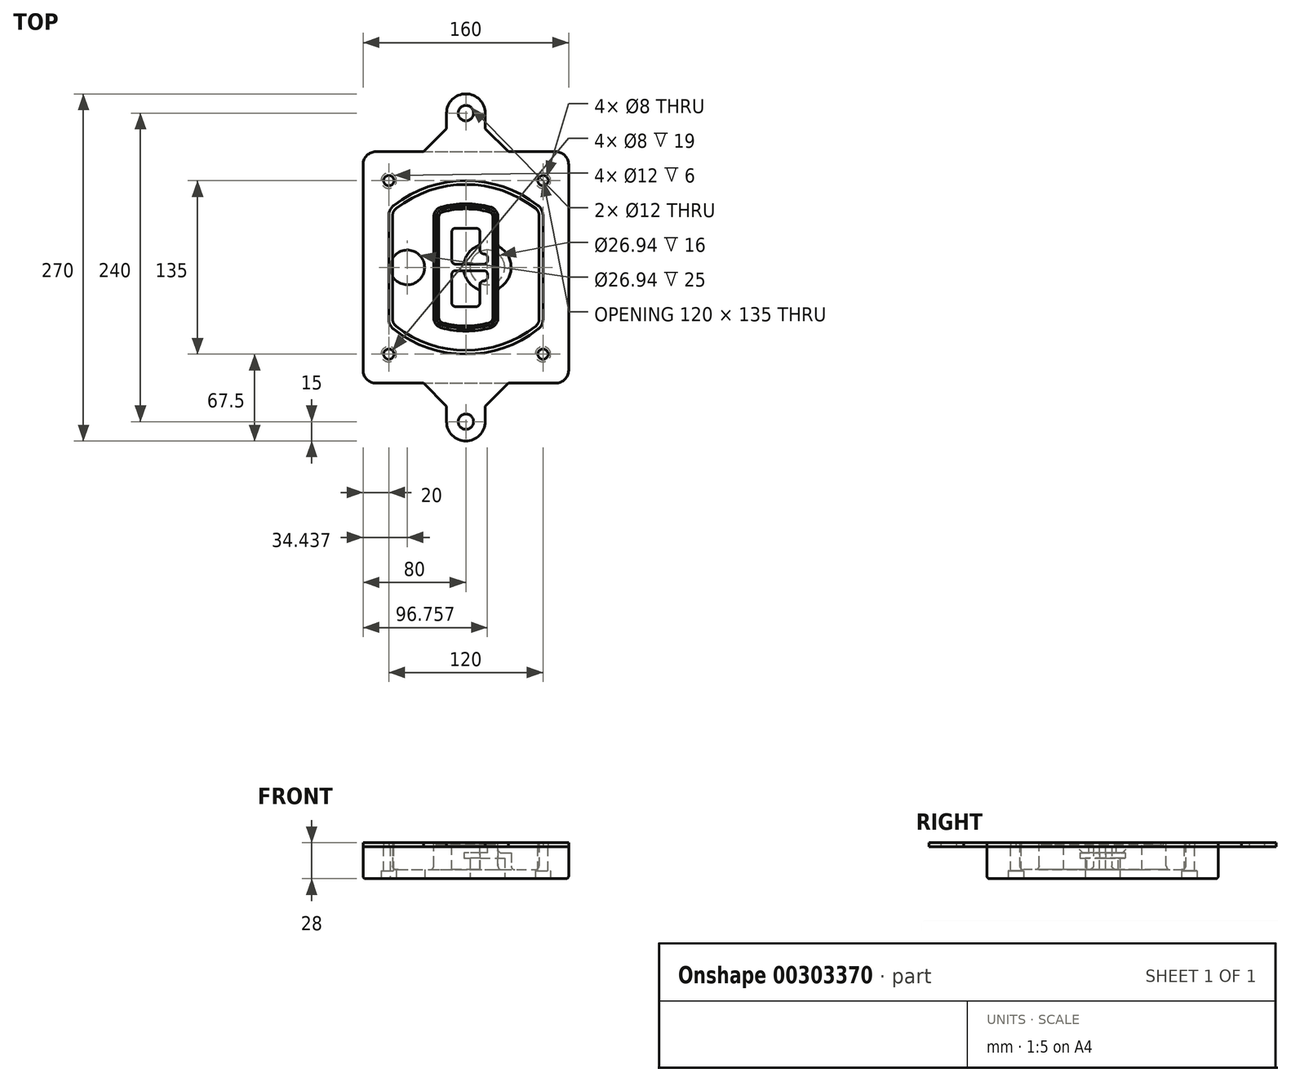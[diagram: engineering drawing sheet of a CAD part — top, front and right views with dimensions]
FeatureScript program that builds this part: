
annotation { "Feature Type Name" : "Feature", "Feature Type Description" : "" }
export const myFeature = defineFeature(function(context is Context, id is Id, definition is map)
    precondition{}
    {
        {
            var Q0;
            Q0=qCreatedBy(makeId("Top.planeOp"),FACE);
            var sketch = newSketch(context, id + "F0", { "sketchPlane" : qUnion([Q0])});
            skPoint(sketch, "E0.rect.middle", {"position": v(0, 0) * mm});
            skLineSegment(sketch, "E1.bottom", {"start": v(-70, -90) * mm, "end": v(70, -90) * mm});
            skLineSegment(sketch, "E1.top", {"start": v(-70, 90) * mm, "end": v(70, 90) * mm});
            skLineSegment(sketch, "E1.left", {"start": v(-80, -80) * mm, "end": v(-80, 80) * mm});
            skLineSegment(sketch, "E1.right", {"start": v(80, -80) * mm, "end": v(80, 80) * mm});
            skLineSegment(sketch, "E2", {"start": v(-80, 90) * mm, "end": v(80, -90) * mm, "construction": true});
            skLineSegment(sketch, "E3", {"start": v(80, 90) * mm, "end": v(-80, -90) * mm, "construction": true});
            skCircle(sketch, "E4", {"center": v(-60, 67.5) * mm, "radius": 4 * mm});
            skCircle(sketch, "E5", {"center": v(60, 67.5) * mm, "radius": 4 * mm});
            skCircle(sketch, "E6", {"center": v(60, -67.5) * mm, "radius": 4 * mm});
            skCircle(sketch, "E7", {"center": v(-60, -67.5) * mm, "radius": 4 * mm});
            skLineSegment(sketch, "E8", {"start": v(-60, 67.5) * mm, "end": v(60, 67.5) * mm, "construction": true});
            skLineSegment(sketch, "E9", {"start": v(60, 67.5) * mm, "end": v(60, -67.5) * mm, "construction": true});
            skLineSegment(sketch, "E10", {"start": v(60, -67.5) * mm, "end": v(-60, -67.5) * mm, "construction": true});
            skLineSegment(sketch, "E11", {"start": v(-60, -67.5) * mm, "end": v(-60, 67.5) * mm, "construction": true});
            skLineSegment(sketch, "E12", {"start": v(-60, 40.3) * mm, "end": v(-60, -40.3) * mm});
            skLineSegment(sketch, "E13", {"start": v(60, 40.3) * mm, "end": v(60, -40.3) * mm});
            skArc(sketch, "E14", {"start": v(56.15, 48.18) * mm, "mid": v(0, 67.5) * mm, "end": v(-56.15, 48.18) * mm});
            skArc(sketch, "E15", {"start": v(-56.15, -48.18) * mm, "mid": v(0, -67.5) * mm, "end": v(56.15, -48.18) * mm});
            skLineSegment(sketch, "E16", {"start": v(-60, 0) * mm, "end": v(60, 0) * mm, "construction": true});
            skPoint(sketch, "E17.visualSharp", {"position": v(-60, -45) * mm});
            skArc(sketch, "E17.filletArc", {"start": v(-60, -40.3) * mm, "mid": v(-58.99, -44.68) * mm, "end": v(-56.15, -48.18) * mm});
            skPoint(sketch, "E18.visualSharp", {"position": v(-60, 45) * mm});
            skArc(sketch, "E18.filletArc", {"start": v(-56.15, 48.18) * mm, "mid": v(-58.99, 44.68) * mm, "end": v(-60, 40.3) * mm});
            skPoint(sketch, "E19.visualSharp", {"position": v(60, 45) * mm});
            skArc(sketch, "E19.filletArc", {"start": v(60, 40.3) * mm, "mid": v(58.99, 44.68) * mm, "end": v(56.15, 48.18) * mm});
            skPoint(sketch, "E20.visualSharp", {"position": v(60, -45) * mm});
            skArc(sketch, "E20.filletArc", {"start": v(56.15, -48.18) * mm, "mid": v(58.99, -44.68) * mm, "end": v(60, -40.3) * mm});
            skPoint(sketch, "E21.visualSharp", {"position": v(-80, 90) * mm});
            skArc(sketch, "E21.filletArc", {"start": v(-70, 90) * mm, "mid": v(-77.07, 87.07) * mm, "end": v(-80, 80) * mm});
            skPoint(sketch, "E22.visualSharp", {"position": v(80, 90) * mm});
            skArc(sketch, "E22.filletArc", {"start": v(80, 80) * mm, "mid": v(77.07, 87.07) * mm, "end": v(70, 90) * mm});
            skPoint(sketch, "E23.visualSharp", {"position": v(80, -90) * mm});
            skArc(sketch, "E23.filletArc", {"start": v(70, -90) * mm, "mid": v(77.07, -87.07) * mm, "end": v(80, -80) * mm});
            skPoint(sketch, "E24.visualSharp", {"position": v(-80, -90) * mm});
            skArc(sketch, "E24.filletArc", {"start": v(-80, -80) * mm, "mid": v(-77.07, -87.07) * mm, "end": v(-70, -90) * mm});
            skArc(sketch, "E25.0", {"start": v(57, 40.3) * mm, "mid": v(56.3, 43.36) * mm, "end": v(54.3, 45.81) * mm});
            skLineSegment(sketch, "E25.1", {"start": v(57, 40.3) * mm, "end": v(57, -40.3) * mm});
            skArc(sketch, "E25.2", {"start": v(54.3, -45.81) * mm, "mid": v(56.3, -43.36) * mm, "end": v(57, -40.3) * mm});
            skArc(sketch, "E25.3", {"start": v(-54.3, -45.81) * mm, "mid": v(0, -64.5) * mm, "end": v(54.3, -45.81) * mm});
            skArc(sketch, "E25.4", {"start": v(-57, -40.3) * mm, "mid": v(-56.3, -43.36) * mm, "end": v(-54.3, -45.81) * mm});
            skArc(sketch, "E25.5", {"start": v(54.3, 45.81) * mm, "mid": v(0, 64.5) * mm, "end": v(-54.3, 45.81) * mm});
            skLineSegment(sketch, "E25.6", {"start": v(-57, 40.3) * mm, "end": v(-57, -40.3) * mm});
            skArc(sketch, "E25.7", {"start": v(-54.3, 45.81) * mm, "mid": v(-56.3, 43.36) * mm, "end": v(-57, 40.3) * mm});
            skArc(sketch, "E26.0", {"start": v(-58.62, 51.33) * mm, "mid": v(-62.58, 46.43) * mm, "end": v(-64, 40.3) * mm});
            skArc(sketch, "E26.1", {"start": v(58.62, 51.33) * mm, "mid": v(0, 71.5) * mm, "end": v(-58.62, 51.33) * mm});
            skArc(sketch, "E26.2", {"start": v(64, 40.3) * mm, "mid": v(62.58, 46.43) * mm, "end": v(58.62, 51.33) * mm});
            skLineSegment(sketch, "E26.3", {"start": v(64, 40.3) * mm, "end": v(64, -40.3) * mm});
            skArc(sketch, "E26.4", {"start": v(58.62, -51.33) * mm, "mid": v(62.58, -46.43) * mm, "end": v(64, -40.3) * mm});
            skLineSegment(sketch, "E26.5", {"start": v(-64, 40.3) * mm, "end": v(-64, -40.3) * mm});
            skArc(sketch, "E26.6", {"start": v(-58.62, -51.33) * mm, "mid": v(0, -71.5) * mm, "end": v(58.62, -51.33) * mm});
            skArc(sketch, "E26.7", {"start": v(-64, -40.3) * mm, "mid": v(-62.58, -46.43) * mm, "end": v(-58.62, -51.33) * mm});
            skSolve(sketch);
        }
        {
            var Q0;
            Q0=makeQuery(id+"F0.imprint","IMPRINT",FACE,{"disambiguationData":[TD([[makeQuery(id+"F0.imprint","IMPRINT",EDGE,{"derivedFrom":sQuery(id+"F0.wireOp",EDGE,"E1.bottom")}),1.0]])]});
            var Q1;
            Q1=makeQuery(id+"F0.imprint","IMPRINT",FACE,{"disambiguationData":[TD([[makeQuery(id+"F0.imprint","IMPRINT",EDGE,{"derivedFrom":sQuery(id+"F0.wireOp",EDGE,"E12")}),1.0]])]});
            var Q2;
            Q2=makeQuery(id+"F0.imprint","IMPRINT",FACE,{"disambiguationData":[TD([[makeQuery(id+"F0.imprint","IMPRINT",EDGE,{"derivedFrom":sQuery(id+"F0.wireOp",EDGE,"E25.0")}),1.0]])]});
            var Q3;
            Q3=makeQuery(id+"F0.imprint","IMPRINT",FACE,{"disambiguationData":[TD([[makeQuery(id+"F0.imprint","IMPRINT",EDGE,{"derivedFrom":sQuery(id+"F0.wireOp",EDGE,"E12")}),-1.0]])]});
            extrude(context, id + "F1", {"entities" : qUnion([Q0, Q1, Q2, Q3]), "oppositeDirection" : true, "depth" : 25 * mm});
        }
        {
            var Q0;
            Q0=makeQuery(id+"F0.imprint","IMPRINT",FACE,{"disambiguationData":[TD([[makeQuery(id+"F0.imprint","IMPRINT",EDGE,{"derivedFrom":sQuery(id+"F0.wireOp",EDGE,"E12")}),1.0]])]});
            extrude(context, id + "F2", {"entities" : qUnion([Q0]), "operationType" : NewBodyOperationType.ADD, "depth" : 3 * mm});
        }
        {
            var Q0;
            Q0=makeQuery(id+"F0.imprint","IMPRINT",FACE,{"disambiguationData":[TD([[makeQuery(id+"F0.imprint","IMPRINT",EDGE,{"derivedFrom":sQuery(id+"F0.wireOp",EDGE,"E25.0")}),1.0]])]});
            extrude(context, id + "F3", {"entities" : qUnion([Q0]), "operationType" : NewBodyOperationType.REMOVE, "oppositeDirection" : true, "depth" : 18 * mm});
        }
        {
            var Q0;
            Q0=makeQuery(id+"F2.opExtrude","CAP_FACE",FACE,{"disambiguationData":[OSD([sQuery(id+"F0.wireOp",EDGE,"E12"),sQuery(id+"F0.wireOp",EDGE,"E13"),sQuery(id+"F0.wireOp",EDGE,"E14"),sQuery(id+"F0.wireOp",EDGE,"E15"),sQuery(id+"F0.wireOp",EDGE,"E17.filletArc"),sQuery(id+"F0.wireOp",EDGE,"E18.filletArc"),sQuery(id+"F0.wireOp",EDGE,"E19.filletArc"),sQuery(id+"F0.wireOp",EDGE,"E20.filletArc"),sQuery(id+"F0.wireOp",EDGE,"E25.0"),sQuery(id+"F0.wireOp",EDGE,"E25.1"),sQuery(id+"F0.wireOp",EDGE,"E25.2"),sQuery(id+"F0.wireOp",EDGE,"E25.3"),sQuery(id+"F0.wireOp",EDGE,"E25.4"),sQuery(id+"F0.wireOp",EDGE,"E25.5"),sQuery(id+"F0.wireOp",EDGE,"E25.6"),sQuery(id+"F0.wireOp",EDGE,"E25.7")])],"isStart":false});
            var sketch = newSketch(context, id + "F4", { "sketchPlane" : qUnion([Q0])});
            skArc(sketch, "E27.0", {"start": v(-19.08, -46.97) * mm, "mid": v(0, -49.5) * mm, "end": v(19.08, -46.97) * mm});
            skArc(sketch, "E28.0", {"start": v(19.08, 46.97) * mm, "mid": v(0, 49.5) * mm, "end": v(-19.08, 46.97) * mm});
            skLineSegment(sketch, "E29", {"start": v(-25, 39.25) * mm, "end": v(-25, -39.25) * mm});
            skLineSegment(sketch, "E30", {"start": v(25, 39.25) * mm, "end": v(25, -39.25) * mm});
            skLineSegment(sketch, "E31", {"start": v(-25, 45.1) * mm, "end": v(25, 45.1) * mm, "construction": true});
            skLineSegment(sketch, "E32", {"start": v(-25, -45.1) * mm, "end": v(25, -45.1) * mm, "construction": true});
            skPoint(sketch, "E33.visualSharp", {"position": v(-25, 45.1) * mm});
            skArc(sketch, "E33.filletArc", {"start": v(-19.08, 46.97) * mm, "mid": v(-23.35, 44.11) * mm, "end": v(-25, 39.25) * mm});
            skPoint(sketch, "E34.visualSharp", {"position": v(25, 45.1) * mm});
            skArc(sketch, "E34.filletArc", {"start": v(25, 39.25) * mm, "mid": v(23.35, 44.11) * mm, "end": v(19.08, 46.97) * mm});
            skPoint(sketch, "E35.visualSharp", {"position": v(25, -45.1) * mm});
            skArc(sketch, "E35.filletArc", {"start": v(19.08, -46.97) * mm, "mid": v(23.35, -44.11) * mm, "end": v(25, -39.25) * mm});
            skPoint(sketch, "E36.visualSharp", {"position": v(-25, -45.1) * mm});
            skArc(sketch, "E36.filletArc", {"start": v(-25, -39.25) * mm, "mid": v(-23.35, -44.11) * mm, "end": v(-19.08, -46.97) * mm});
            skArc(sketch, "E37.0", {"start": v(54.3, 45.81) * mm, "mid": v(0, 64.5) * mm, "end": v(-54.3, 45.81) * mm});
            skArc(sketch, "E37.1", {"start": v(-54.3, 45.81) * mm, "mid": v(-56.3, 43.36) * mm, "end": v(-57, 40.3) * mm});
            skLineSegment(sketch, "E37.2", {"start": v(-57, 40.3) * mm, "end": v(-57, -40.3) * mm});
            skArc(sketch, "E37.3", {"start": v(-57, -40.3) * mm, "mid": v(-56.3, -43.36) * mm, "end": v(-54.3, -45.81) * mm});
            skArc(sketch, "E37.4", {"start": v(-54.3, -45.81) * mm, "mid": v(0, -64.5) * mm, "end": v(54.3, -45.81) * mm});
            skArc(sketch, "E37.5", {"start": v(54.3, -45.81) * mm, "mid": v(56.3, -43.36) * mm, "end": v(57, -40.3) * mm});
            skLineSegment(sketch, "E37.6", {"start": v(57, 40.3) * mm, "end": v(57, -40.3) * mm});
            skArc(sketch, "E37.7", {"start": v(57, 40.3) * mm, "mid": v(56.3, 43.36) * mm, "end": v(54.3, 45.81) * mm});
            skLineSegment(sketch, "E38.0", {"start": v(23, 39.25) * mm, "end": v(23, -39.25) * mm});
            skArc(sketch, "E38.1", {"start": v(18.56, -45.04) * mm, "mid": v(21.76, -42.9) * mm, "end": v(23, -39.25) * mm});
            skArc(sketch, "E38.2", {"start": v(-18.56, -45.04) * mm, "mid": v(0, -47.5) * mm, "end": v(18.56, -45.04) * mm});
            skArc(sketch, "E38.3", {"start": v(-23, -39.25) * mm, "mid": v(-21.76, -42.9) * mm, "end": v(-18.56, -45.04) * mm});
            skLineSegment(sketch, "E38.4", {"start": v(-23, 39.25) * mm, "end": v(-23, -39.25) * mm});
            skArc(sketch, "E38.5", {"start": v(23, 39.25) * mm, "mid": v(21.76, 42.9) * mm, "end": v(18.56, 45.04) * mm});
            skArc(sketch, "E38.6", {"start": v(-18.56, 45.04) * mm, "mid": v(-21.76, 42.9) * mm, "end": v(-23, 39.25) * mm});
            skArc(sketch, "E38.7", {"start": v(18.56, 45.04) * mm, "mid": v(0, 47.5) * mm, "end": v(-18.56, 45.04) * mm});
            skArc(sketch, "E39.0", {"start": v(21, 39.25) * mm, "mid": v(20.18, 41.68) * mm, "end": v(18.04, 43.1) * mm});
            skLineSegment(sketch, "E39.1", {"start": v(21, 39.25) * mm, "end": v(21, -39.25) * mm});
            skArc(sketch, "E39.2", {"start": v(18.04, -43.1) * mm, "mid": v(20.18, -41.68) * mm, "end": v(21, -39.25) * mm});
            skArc(sketch, "E39.3", {"start": v(-18.04, -43.1) * mm, "mid": v(0, -45.5) * mm, "end": v(18.04, -43.1) * mm});
            skArc(sketch, "E39.4", {"start": v(-21, -39.25) * mm, "mid": v(-20.18, -41.68) * mm, "end": v(-18.04, -43.1) * mm});
            skArc(sketch, "E39.5", {"start": v(18.04, 43.1) * mm, "mid": v(0, 45.5) * mm, "end": v(-18.04, 43.1) * mm});
            skLineSegment(sketch, "E39.6", {"start": v(-21, 39.25) * mm, "end": v(-21, -39.25) * mm});
            skArc(sketch, "E39.7", {"start": v(-18.04, 43.1) * mm, "mid": v(-20.18, 41.68) * mm, "end": v(-21, 39.25) * mm});
            skLineSegment(sketch, "E40", {"start": v(-25, 0) * mm, "end": v(25, 0) * mm, "construction": true});
            skLineSegment(sketch, "E41", {"start": v(-11, 5.5) * mm, "end": v(-11, 27.5) * mm});
            skLineSegment(sketch, "E42", {"start": v(-8, 30.5) * mm, "end": v(8, 30.5) * mm});
            skLineSegment(sketch, "E43", {"start": v(11, 27.5) * mm, "end": v(11, 13.5) * mm});
            skLineSegment(sketch, "E44", {"start": v(14, 10.5) * mm, "end": v(14, 10.5) * mm});
            skLineSegment(sketch, "E45", {"start": v(17, 7.5) * mm, "end": v(17, 5.5) * mm});
            skLineSegment(sketch, "E46", {"start": v(14, 2.5) * mm, "end": v(-8, 2.5) * mm});
            skPoint(sketch, "E47.visualSharp", {"position": v(-11, 30.5) * mm});
            skArc(sketch, "E47.filletArc", {"start": v(-8, 30.5) * mm, "mid": v(-10.12, 29.62) * mm, "end": v(-11, 27.5) * mm});
            skPoint(sketch, "E48.visualSharp", {"position": v(11, 30.5) * mm});
            skArc(sketch, "E48.filletArc", {"start": v(11, 27.5) * mm, "mid": v(10.12, 29.62) * mm, "end": v(8, 30.5) * mm});
            skPoint(sketch, "E49.visualSharp", {"position": v(11, 10.5) * mm});
            skArc(sketch, "E49.filletArc", {"start": v(11, 13.5) * mm, "mid": v(11.88, 11.38) * mm, "end": v(14, 10.5) * mm});
            skPoint(sketch, "E50.visualSharp", {"position": v(17, 10.5) * mm});
            skArc(sketch, "E50.filletArc", {"start": v(17, 7.5) * mm, "mid": v(16.12, 9.62) * mm, "end": v(14, 10.5) * mm});
            skPoint(sketch, "E51.visualSharp", {"position": v(17, 2.5) * mm});
            skArc(sketch, "E51.filletArc", {"start": v(14, 2.5) * mm, "mid": v(16.12, 3.38) * mm, "end": v(17, 5.5) * mm});
            skPoint(sketch, "E52.visualSharp", {"position": v(-11, 2.5) * mm});
            skArc(sketch, "E52.filletArc", {"start": v(-11, 5.5) * mm, "mid": v(-10.12, 3.38) * mm, "end": v(-8, 2.5) * mm});
            skLineSegment(sketch, "E53.0.MirrorCS", {"start": v(14, -2.5) * mm, "end": v(-8, -2.5) * mm});
            skArc(sketch, "E54.0.MirrorCS", {"start": v(-11, -5.5) * mm, "mid": v(-10.12, -3.38) * mm, "end": v(-8, -2.5) * mm});
            skLineSegment(sketch, "E55.0.MirrorCS", {"start": v(-11, -5.5) * mm, "end": v(-11, -27.5) * mm});
            skArc(sketch, "E56.0.MirrorCS", {"start": v(-8, -30.5) * mm, "mid": v(-10.12, -29.62) * mm, "end": v(-11, -27.5) * mm});
            skLineSegment(sketch, "E57.0.MirrorCS", {"start": v(-8, -30.5) * mm, "end": v(8, -30.5) * mm});
            skArc(sketch, "E58.0.MirrorCS", {"start": v(11, -27.5) * mm, "mid": v(10.12, -29.62) * mm, "end": v(8, -30.5) * mm});
            skLineSegment(sketch, "E59.0.MirrorCS", {"start": v(11, -27.5) * mm, "end": v(11, -13.5) * mm});
            skArc(sketch, "E60.0.MirrorCS", {"start": v(11, -13.5) * mm, "mid": v(11.88, -11.38) * mm, "end": v(14, -10.5) * mm});
            skArc(sketch, "E61.0.MirrorCS", {"start": v(17, -7.5) * mm, "mid": v(16.12, -9.62) * mm, "end": v(14, -10.5) * mm});
            skLineSegment(sketch, "E62.0.MirrorCS", {"start": v(17, -7.5) * mm, "end": v(17, -5.5) * mm});
            skArc(sketch, "E63.0.MirrorCS", {"start": v(14, -2.5) * mm, "mid": v(16.12, -3.38) * mm, "end": v(17, -5.5) * mm});
            skSolve(sketch);
        }
        {
            var Q0;
            Q0=makeQuery(id+"F4.imprint","IMPRINT",FACE,{"disambiguationData":[TD([[makeQuery(id+"F4.imprint","IMPRINT",EDGE,{"derivedFrom":sQuery(id+"F4.wireOp",EDGE,"E27.0")}),1.0]])]});
            var Q1;
            Q1=makeQuery(id+"F4.imprint","IMPRINT",FACE,{"disambiguationData":[TD([[makeQuery(id+"F4.imprint","IMPRINT",EDGE,{"derivedFrom":sQuery(id+"F4.wireOp",EDGE,"E38.0")}),-1.0]])]});
            var Q2;
            Q2=makeQuery(id+"F4.imprint","IMPRINT",FACE,{"disambiguationData":[TD([[makeQuery(id+"F4.imprint","IMPRINT",EDGE,{"derivedFrom":sQuery(id+"F4.wireOp",EDGE,"E39.0")}),1.0]])]});
            extrude(context, id + "F5", {"entities" : qUnion([Q0, Q1, Q2]), "operationType" : NewBodyOperationType.ADD, "endBound" : BoundingType.UP_TO_NEXT, "oppositeDirection" : true, "depth" : 25 * mm});
        }
        {
            var Q0;
            Q0=makeQuery(id+"F4.imprint","IMPRINT",FACE,{"disambiguationData":[TD([[makeQuery(id+"F4.imprint","IMPRINT",EDGE,{"derivedFrom":sQuery(id+"F4.wireOp",EDGE,"E38.0")}),-1.0]])]});
            extrude(context, id + "F6", {"entities" : qUnion([Q0]), "operationType" : NewBodyOperationType.REMOVE, "oppositeDirection" : true, "depth" : 2 * mm});
        }
        {
            var Q0;
            Q0=makeQuery(id+"F1.opExtrude","CAP_FACE",FACE,{"disambiguationData":[OSD([sQuery(id+"F0.wireOp",EDGE,"E1.bottom"),sQuery(id+"F0.wireOp",EDGE,"E1.top"),sQuery(id+"F0.wireOp",EDGE,"E1.left"),sQuery(id+"F0.wireOp",EDGE,"E1.right"),sQuery(id+"F0.wireOp",EDGE,"E4"),sQuery(id+"F0.wireOp",EDGE,"E5"),sQuery(id+"F0.wireOp",EDGE,"E6"),sQuery(id+"F0.wireOp",EDGE,"E7"),sQuery(id+"F0.wireOp",EDGE,"E21.filletArc"),sQuery(id+"F0.wireOp",EDGE,"E22.filletArc"),sQuery(id+"F0.wireOp",EDGE,"E23.filletArc"),sQuery(id+"F0.wireOp",EDGE,"E24.filletArc")])],"isStart":false});
            var sketch = newSketch(context, id + "F7", { "sketchPlane" : qUnion([Q0])});
            skCircle(sketch, "E64", {"center": v(16.76, 0) * mm, "radius": 13.47 * mm});
            skCircle(sketch, "E65", {"center": v(-45.56, 0) * mm, "radius": 13.47 * mm});
            skLineSegment(sketch, "E66", {"start": v(80, 0) * mm, "end": v(-80, 0) * mm});
            skCircle(sketch, "E67", {"center": v(16.76, 0) * mm, "radius": 18.47 * mm});
            skCircle(sketch, "E68", {"center": v(60, -67.5) * mm, "radius": 6 * mm});
            skCircle(sketch, "E69", {"center": v(-60, -67.5) * mm, "radius": 6 * mm});
            skCircle(sketch, "E70", {"center": v(-60, 67.5) * mm, "radius": 6 * mm});
            skCircle(sketch, "E71", {"center": v(60, 67.5) * mm, "radius": 6 * mm});
            skSolve(sketch);
        }
        {
            var Q0;
            {var subQ1=sQuery(id+"F7.wireOp",EDGE,"E66");var subQ4=sQuery(id+"F7.wireOp",EDGE,"E64");var subQ6=makeQuery(id+"F7.imprint","INTERSECT",VERTEX,{"disambiguationData":[OD(0.0)],"derivedFrom":[subQ4,subQ1]});Q0=makeQuery(id+"F7.imprint","IMPRINT",FACE,{"disambiguationData":[TD([[makeQuery(id+"F7.imprint","IMPRINT",EDGE,{"disambiguationData":[TD([[subQ6,-1.0]])],"derivedFrom":subQ4}),-1.0]])]});}
            var Q1;
            {var subQ0=sQuery(id+"F7.wireOp",EDGE,"E66");var subQ1=sQuery(id+"F7.wireOp",EDGE,"E64");var subQ3=makeQuery(id+"F7.imprint","INTERSECT",VERTEX,{"disambiguationData":[OD(0.0)],"derivedFrom":[subQ1,subQ0]});Q1=makeQuery(id+"F7.imprint","IMPRINT",FACE,{"disambiguationData":[TD([[makeQuery(id+"F7.imprint","IMPRINT",EDGE,{"disambiguationData":[TD([[subQ3,-1.0]])],"derivedFrom":subQ1}),1.0]])]});}
            var Q2;
            {var subQ0=sQuery(id+"F7.wireOp",EDGE,"E66");var subQ1=sQuery(id+"F7.wireOp",EDGE,"E64");var subQ3=makeQuery(id+"F7.imprint","INTERSECT",VERTEX,{"disambiguationData":[OD(0.0)],"derivedFrom":[subQ1,subQ0]});Q2=makeQuery(id+"F7.imprint","IMPRINT",FACE,{"disambiguationData":[TD([[makeQuery(id+"F7.imprint","IMPRINT",EDGE,{"disambiguationData":[TD([[subQ3,1.0]])],"derivedFrom":subQ1}),1.0]])]});}
            var Q3;
            {var subQ1=sQuery(id+"F7.wireOp",EDGE,"E66");var subQ4=sQuery(id+"F7.wireOp",EDGE,"E64");var subQ6=makeQuery(id+"F7.imprint","INTERSECT",VERTEX,{"disambiguationData":[OD(0.0)],"derivedFrom":[subQ4,subQ1]});Q3=makeQuery(id+"F7.imprint","IMPRINT",FACE,{"disambiguationData":[TD([[makeQuery(id+"F7.imprint","IMPRINT",EDGE,{"disambiguationData":[TD([[subQ6,1.0]])],"derivedFrom":subQ4}),-1.0]])]});}
            extrude(context, id + "F8", {"entities" : qUnion([Q0, Q1, Q2, Q3]), "operationType" : NewBodyOperationType.ADD, "oppositeDirection" : true, "depth" : 20 * mm});
        }
        {
            var Q0;
            {var subQ0=sQuery(id+"F7.wireOp",EDGE,"E66");var subQ1=sQuery(id+"F7.wireOp",EDGE,"E64");var subQ3=makeQuery(id+"F7.imprint","INTERSECT",VERTEX,{"disambiguationData":[OD(0.0)],"derivedFrom":[subQ1,subQ0]});Q0=makeQuery(id+"F7.imprint","IMPRINT",FACE,{"disambiguationData":[TD([[makeQuery(id+"F7.imprint","IMPRINT",EDGE,{"disambiguationData":[TD([[subQ3,-1.0]])],"derivedFrom":subQ1}),1.0]])]});}
            var Q1;
            {var subQ0=sQuery(id+"F7.wireOp",EDGE,"E66");var subQ1=sQuery(id+"F7.wireOp",EDGE,"E64");var subQ3=makeQuery(id+"F7.imprint","INTERSECT",VERTEX,{"disambiguationData":[OD(0.0)],"derivedFrom":[subQ1,subQ0]});Q1=makeQuery(id+"F7.imprint","IMPRINT",FACE,{"disambiguationData":[TD([[makeQuery(id+"F7.imprint","IMPRINT",EDGE,{"disambiguationData":[TD([[subQ3,1.0]])],"derivedFrom":subQ1}),1.0]])]});}
            extrude(context, id + "F9", {"entities" : qUnion([Q0, Q1]), "operationType" : NewBodyOperationType.REMOVE, "oppositeDirection" : true, "depth" : 16 * mm});
        }
        {
            var Q0;
            {var subQ0=sQuery(id+"F7.wireOp",EDGE,"E66");var subQ1=sQuery(id+"F7.wireOp",EDGE,"E65");var subQ3=makeQuery(id+"F7.imprint","INTERSECT",VERTEX,{"disambiguationData":[OD(0.0)],"derivedFrom":[subQ1,subQ0]});Q0=makeQuery(id+"F7.imprint","IMPRINT",FACE,{"disambiguationData":[TD([[makeQuery(id+"F7.imprint","IMPRINT",EDGE,{"disambiguationData":[TD([[subQ3,-1.0]])],"derivedFrom":subQ1}),1.0]])]});}
            var Q1;
            {var subQ0=sQuery(id+"F7.wireOp",EDGE,"E66");var subQ1=sQuery(id+"F7.wireOp",EDGE,"E65");var subQ3=makeQuery(id+"F7.imprint","INTERSECT",VERTEX,{"disambiguationData":[OD(0.0)],"derivedFrom":[subQ1,subQ0]});Q1=makeQuery(id+"F7.imprint","IMPRINT",FACE,{"disambiguationData":[TD([[makeQuery(id+"F7.imprint","IMPRINT",EDGE,{"disambiguationData":[TD([[subQ3,1.0]])],"derivedFrom":subQ1}),1.0]])]});}
            extrude(context, id + "F10", {"entities" : qUnion([Q0, Q1]), "operationType" : NewBodyOperationType.REMOVE, "oppositeDirection" : true, "depth" : 25 * mm});
        }
        {
            var Q0;
            Q0=makeQuery(id+"F7.imprint","IMPRINT",FACE,{"disambiguationData":[TD([[makeQuery(id+"F7.imprint","IMPRINT",EDGE,{"derivedFrom":sQuery(id+"F7.wireOp",EDGE,"E68")}),1.0]])]});
            var Q1;
            Q1=makeQuery(id+"F7.imprint","IMPRINT",FACE,{"disambiguationData":[TD([[makeQuery(id+"F7.imprint","IMPRINT",EDGE,{"derivedFrom":makeQuery(id+"F1.opExtrude","CAP_EDGE",EDGE,{"disambiguationData":[OSD([sQuery(id+"F0.wireOp",EDGE,"E5")])],"isStart":false})}),-1.0]])]});
            var Q2;
            Q2=makeQuery(id+"F7.imprint","IMPRINT",FACE,{"disambiguationData":[TD([[makeQuery(id+"F7.imprint","IMPRINT",EDGE,{"derivedFrom":sQuery(id+"F7.wireOp",EDGE,"E69")}),1.0]])]});
            var Q3;
            Q3=makeQuery(id+"F7.imprint","IMPRINT",FACE,{"disambiguationData":[TD([[makeQuery(id+"F7.imprint","IMPRINT",EDGE,{"derivedFrom":makeQuery(id+"F1.opExtrude","CAP_EDGE",EDGE,{"disambiguationData":[OSD([sQuery(id+"F0.wireOp",EDGE,"E4")])],"isStart":false})}),-1.0]])]});
            var Q4;
            Q4=makeQuery(id+"F7.imprint","IMPRINT",FACE,{"disambiguationData":[TD([[makeQuery(id+"F7.imprint","IMPRINT",EDGE,{"derivedFrom":sQuery(id+"F7.wireOp",EDGE,"E70")}),1.0]])]});
            var Q5;
            Q5=makeQuery(id+"F7.imprint","IMPRINT",FACE,{"disambiguationData":[TD([[makeQuery(id+"F7.imprint","IMPRINT",EDGE,{"derivedFrom":makeQuery(id+"F1.opExtrude","CAP_EDGE",EDGE,{"disambiguationData":[OSD([sQuery(id+"F0.wireOp",EDGE,"E7")])],"isStart":false})}),-1.0]])]});
            var Q6;
            Q6=makeQuery(id+"F7.imprint","IMPRINT",FACE,{"disambiguationData":[TD([[makeQuery(id+"F7.imprint","IMPRINT",EDGE,{"derivedFrom":sQuery(id+"F7.wireOp",EDGE,"E71")}),1.0]])]});
            var Q7;
            Q7=makeQuery(id+"F7.imprint","IMPRINT",FACE,{"disambiguationData":[TD([[makeQuery(id+"F7.imprint","IMPRINT",EDGE,{"derivedFrom":makeQuery(id+"F1.opExtrude","CAP_EDGE",EDGE,{"disambiguationData":[OSD([sQuery(id+"F0.wireOp",EDGE,"E6")])],"isStart":false})}),-1.0]])]});
            extrude(context, id + "F11", {"entities" : qUnion([Q0, Q1, Q2, Q3, Q4, Q5, Q6, Q7]), "operationType" : NewBodyOperationType.REMOVE, "oppositeDirection" : true, "depth" : 6 * mm});
        }
        {
            var Q0;
            Q0=makeQuery(id+"F9.boolean.opBoolean","COPY",FACE,{"derivedFrom":makeQuery(id+"F9.opExtrude","CAP_FACE",FACE,{"disambiguationData":[OSD([sQuery(id+"F7.wireOp",EDGE,"E64")])],"isStart":false})});
            var sketch = newSketch(context, id + "F12", { "sketchPlane" : qUnion([Q0])});
            skArc(sketch, "E72.0", {"start": v(11, 17.55) * mm, "mid": v(2.57, 11.82) * mm, "end": v(-1.54, 2.5) * mm});
            skArc(sketch, "E72.1", {"start": v(-1.54, -2.5) * mm, "mid": v(2.57, -11.82) * mm, "end": v(11, -17.55) * mm});
            skLineSegment(sketch, "E73", {"start": v(-1.54, -2.5) * mm, "end": v(14, -2.5) * mm});
            skLineSegment(sketch, "E74.0", {"start": v(14, 2.5) * mm, "end": v(-1.54, 2.5) * mm});
            skArc(sketch, "E74.1", {"start": v(14, 2.5) * mm, "mid": v(16.12, 3.38) * mm, "end": v(17, 5.5) * mm});
            skLineSegment(sketch, "E74.2", {"start": v(17, 7.5) * mm, "end": v(17, 5.5) * mm});
            skArc(sketch, "E74.3", {"start": v(17, 7.5) * mm, "mid": v(16.12, 9.62) * mm, "end": v(14, 10.5) * mm});
            skArc(sketch, "E74.4", {"start": v(11, 13.5) * mm, "mid": v(11.88, 11.38) * mm, "end": v(14, 10.5) * mm});
            skLineSegment(sketch, "E74.5", {"start": v(11, 17.55) * mm, "end": v(11, 13.5) * mm});
            skLineSegment(sketch, "E74.7", {"start": v(14, -2.5) * mm, "end": v(-1.54, -2.5) * mm});
            skArc(sketch, "E74.8", {"start": v(14, -2.5) * mm, "mid": v(16.12, -3.38) * mm, "end": v(17, -5.5) * mm});
            skLineSegment(sketch, "E74.9", {"start": v(17, -7.5) * mm, "end": v(17, -5.5) * mm});
            skArc(sketch, "E74.10", {"start": v(17, -7.5) * mm, "mid": v(16.12, -9.62) * mm, "end": v(14, -10.5) * mm});
            skArc(sketch, "E74.11", {"start": v(11, -13.5) * mm, "mid": v(11.88, -11.38) * mm, "end": v(14, -10.5) * mm});
            skLineSegment(sketch, "E74.12", {"start": v(11, -17.55) * mm, "end": v(11, -13.5) * mm});
            skPoint(sketch, "E75.orphan", {"position": v(11, -27.5) * mm});
            skPoint(sketch, "E76.orphan", {"position": v(-8, -2.5) * mm});
            skPoint(sketch, "E77.orphan", {"position": v(-8, 2.5) * mm});
            skPoint(sketch, "E78.orphan", {"position": v(11, 27.5) * mm});
            skSolve(sketch);
        }
        {
            var Q0;
            {var subQ7=sQuery(id+"F12.wireOp",EDGE,"E72.0");var subQ14=sQuery(id+"F12.wireOp",EDGE,"E72.1");var subQ16=sQuery(id+"F12.wireOp",EDGE,"E74.1");var subQ18=sQuery(id+"F12.wireOp",EDGE,"E74.8");Q0=qUnion([makeQuery(id+"F12.imprint","IMPRINT",FACE,{"disambiguationData":[TD([[makeQuery(id+"F12.imprint","IMPRINT",EDGE,{"derivedFrom":subQ7}),1.0]])]}),makeQuery(id+"F12.imprint","IMPRINT",FACE,{"disambiguationData":[TD([[makeQuery(id+"F12.imprint","IMPRINT",EDGE,{"derivedFrom":subQ14}),1.0]])]}),makeQuery(id+"F12.imprint","IMPRINT",FACE,{"disambiguationData":[TD([[makeQuery(id+"F12.imprint","IMPRINT",EDGE,{"derivedFrom":subQ16}),1.0]])]}),makeQuery(id+"F12.imprint","IMPRINT",FACE,{"disambiguationData":[TD([[makeQuery(id+"F12.imprint","IMPRINT",EDGE,{"derivedFrom":subQ18}),-1.0]])]})]);}
            var Q1;
            Q1=makeQuery(id+"F5.boolean.opBoolean","SPLIT",FACE,{"disambiguationData":[TD([makeQuery(id+"F5.opExtrude","SWEPT_FACE",FACE,{"disambiguationData":[OSD([sQuery(id+"F4.wireOp",EDGE,"E41")])]})])],"derivedFrom":makeQuery(id+"F3.boolean.opBoolean","COPY",FACE,{"derivedFrom":makeQuery(id+"F3.opExtrude","CAP_FACE",FACE,{"disambiguationData":[OSD([sQuery(id+"F0.wireOp",EDGE,"E25.0"),sQuery(id+"F0.wireOp",EDGE,"E25.1"),sQuery(id+"F0.wireOp",EDGE,"E25.2"),sQuery(id+"F0.wireOp",EDGE,"E25.3"),sQuery(id+"F0.wireOp",EDGE,"E25.4"),sQuery(id+"F0.wireOp",EDGE,"E25.5"),sQuery(id+"F0.wireOp",EDGE,"E25.6"),sQuery(id+"F0.wireOp",EDGE,"E25.7")])],"isStart":false})})});
            extrude(context, id + "F13", {"entities" : qUnion([Q0]), "operationType" : NewBodyOperationType.REMOVE, "endBound" : BoundingType.UP_TO_SURFACE, "endBoundEntityFace" : qUnion([Q1]), "depth" : 25 * mm});
        }
        {
            var Q0;
            Q0=makeQuery(id+"F3.boolean.opBoolean","COPY",EDGE,{"derivedFrom":makeQuery(id+"F3.opExtrude","CAP_EDGE",EDGE,{"disambiguationData":[OSD([sQuery(id+"F0.wireOp",EDGE,"E25.6")])],"isStart":false})});
            var Q1;
            Q1=makeQuery(id+"F8.boolean.opBoolean","INTERSECT",EDGE,{"derivedFrom":[makeQuery(id+"F5.opExtrude","SWEPT_FACE",FACE,{"disambiguationData":[OSD([sQuery(id+"F4.wireOp",EDGE,"E30")])]}),makeQuery(id+"F8.opExtrude","CAP_FACE",FACE,{"disambiguationData":[OSD([sQuery(id+"F7.wireOp",EDGE,"E67")])],"isStart":false})]});
            var Q2;
            Q2=makeQuery(id+"F8.boolean.opBoolean","INTERSECT",EDGE,{"disambiguationData":[OD(1.0)],"derivedFrom":[makeQuery(id+"F5.opExtrude","SWEPT_FACE",FACE,{"disambiguationData":[OSD([sQuery(id+"F4.wireOp",EDGE,"E30")])]}),makeQuery(id+"F8.opExtrude","SWEPT_FACE",FACE,{"disambiguationData":[OSD([sQuery(id+"F7.wireOp",EDGE,"E67")])]})]});
            var Q3;
            {var subQ0=sQuery(id+"F4.wireOp",EDGE,"E30");Q3=makeQuery(id+"F8.boolean.opBoolean","SPLIT",EDGE,{"disambiguationData":[TD([makeQuery(id+"F5.opExtrude","SWEPT_FACE",FACE,{"disambiguationData":[OSD([sQuery(id+"F4.wireOp",EDGE,"E35.filletArc")])]})])],"derivedFrom":makeQuery(id+"F5.opExtrude","CAP_EDGE",EDGE,{"disambiguationData":[OSD([subQ0])],"isStart":false})});}
            var Q4;
            {var subQ0=sQuery(id+"F0.wireOp",EDGE,"E25.7");var subQ1=sQuery(id+"F0.wireOp",EDGE,"E25.1");var subQ2=sQuery(id+"F0.wireOp",EDGE,"E25.6");var subQ3=sQuery(id+"F0.wireOp",EDGE,"E25.5");var subQ4=sQuery(id+"F0.wireOp",EDGE,"E25.4");var subQ5=sQuery(id+"F0.wireOp",EDGE,"E25.0");var subQ6=sQuery(id+"F0.wireOp",EDGE,"E25.2");var subQ7=sQuery(id+"F0.wireOp",EDGE,"E25.3");Q4=makeQuery(id+"F8.boolean.opBoolean","INTERSECT",EDGE,{"derivedFrom":[makeQuery(id+"F5.boolean.opBoolean","SPLIT",FACE,{"disambiguationData":[TD([makeQuery(id+"F2.opExtrude","SWEPT_FACE",FACE,{"disambiguationData":[OSD([subQ5])]})])],"derivedFrom":makeQuery(id+"F3.boolean.opBoolean","COPY",FACE,{"derivedFrom":makeQuery(id+"F3.opExtrude","CAP_FACE",FACE,{"disambiguationData":[OSD([subQ5,subQ1,subQ6,subQ7,subQ4,subQ3,subQ2,subQ0])],"isStart":false})})}),makeQuery(id+"F8.opExtrude","SWEPT_FACE",FACE,{"disambiguationData":[OSD([sQuery(id+"F7.wireOp",EDGE,"E67")])]})]});}
            var Q5;
            Q5=makeQuery(id+"F8.boolean.opBoolean","INTERSECT",EDGE,{"disambiguationData":[OD(0.0)],"derivedFrom":[makeQuery(id+"F5.opExtrude","SWEPT_FACE",FACE,{"disambiguationData":[OSD([sQuery(id+"F4.wireOp",EDGE,"E30")])]}),makeQuery(id+"F8.opExtrude","SWEPT_FACE",FACE,{"disambiguationData":[OSD([sQuery(id+"F7.wireOp",EDGE,"E67")])]})]});
            fillet(context, id + "F14", {"entities" : qUnion([Q0, Q1, Q2, Q3, Q4, Q5]), "radius" : 3 * mm, "tangentPropagation" : true, "allowEdgeOverflow" : false});
        }
        {
            var Q0;
            Q0=makeQuery(id+"F1.opExtrude","CAP_EDGE",EDGE,{"disambiguationData":[OSD([sQuery(id+"F0.wireOp",EDGE,"E1.bottom")])],"isStart":false});
            fillet(context, id + "F15", {"entities" : qUnion([Q0]), "radius" : 2 * mm, "tangentPropagation" : true, "allowEdgeOverflow" : false});
        }
        {
            var Q0;
            {var subQ0=sQuery(id+"F0.wireOp",EDGE,"E21.filletArc");var subQ1=sQuery(id+"F0.wireOp",EDGE,"E7");var subQ2=sQuery(id+"F0.wireOp",EDGE,"E6");var subQ3=sQuery(id+"F0.wireOp",EDGE,"E5");var subQ4=sQuery(id+"F0.wireOp",EDGE,"E4");var subQ5=sQuery(id+"F0.wireOp",EDGE,"E22.filletArc");var subQ6=sQuery(id+"F0.wireOp",EDGE,"E1.bottom");var subQ7=sQuery(id+"F0.wireOp",EDGE,"E1.right");var subQ8=sQuery(id+"F0.wireOp",EDGE,"E1.top");var subQ9=sQuery(id+"F0.wireOp",EDGE,"E1.left");var subQ10=sQuery(id+"F0.wireOp",EDGE,"E23.filletArc");var subQ11=sQuery(id+"F0.wireOp",EDGE,"E24.filletArc");Q0=makeQuery(id+"F2.boolean.opBoolean","SPLIT",FACE,{"disambiguationData":[TD([makeQuery(id+"F1.opExtrude","SWEPT_FACE",FACE,{"disambiguationData":[OSD([subQ6])]})])],"derivedFrom":makeQuery(id+"F1.opExtrude","CAP_FACE",FACE,{"disambiguationData":[OSD([subQ6,subQ8,subQ9,subQ7,subQ4,subQ3,subQ2,subQ1,subQ0,subQ5,subQ10,subQ11])],"isStart":true})});}
            var sketch = newSketch(context, id + "F16", { "sketchPlane" : qUnion([Q0])});
            skLineSegment(sketch, "E79", {"start": v(0, 90) * mm, "end": v(0, 120) * mm, "construction": true});
            skCircle(sketch, "E80", {"center": v(0, 120) * mm, "radius": 6 * mm});
            skArc(sketch, "E81", {"start": v(15, 120) * mm, "mid": v(0, 135) * mm, "end": v(-15, 120) * mm});
            skLineSegment(sketch, "E82", {"start": v(15, 120) * mm, "end": v(15, 108) * mm});
            skLineSegment(sketch, "E83", {"start": v(15, 108) * mm, "end": v(33, 90) * mm});
            skLineSegment(sketch, "E84", {"start": v(-15, 120) * mm, "end": v(-15, 108) * mm});
            skLineSegment(sketch, "E85", {"start": v(-15, 108) * mm, "end": v(-33, 90) * mm});
            skLineSegment(sketch, "E86", {"start": v(-80, 0) * mm, "end": v(80, 0) * mm, "construction": true});
            skLineSegment(sketch, "E87.MirrorCS", {"start": v(15, -108) * mm, "end": v(33, -90) * mm});
            skLineSegment(sketch, "E88.MirrorCS", {"start": v(15, -120) * mm, "end": v(15, -108) * mm});
            skArc(sketch, "E89.MirrorCS", {"start": v(15, -120) * mm, "mid": v(0, -135) * mm, "end": v(-15, -120) * mm});
            skLineSegment(sketch, "E90.MirrorCS", {"start": v(-15, -120) * mm, "end": v(-15, -108) * mm});
            skLineSegment(sketch, "E91.MirrorCS", {"start": v(-15, -108) * mm, "end": v(-33, -90) * mm});
            skLineSegment(sketch, "E92.MirrorCS", {"start": v(0, -90) * mm, "end": v(0, -120) * mm, "construction": true});
            skCircle(sketch, "E93.MirrorC", {"center": v(0, -120) * mm, "radius": 6 * mm});
            skSolve(sketch);
        }
        {
            var Q0;
            Q0=makeQuery(id+"F16.imprint","IMPRINT",FACE,{"disambiguationData":[TD([[makeQuery(id+"F16.imprint","IMPRINT",EDGE,{"derivedFrom":makeQuery(id+"F1.opExtrude","CAP_EDGE",EDGE,{"disambiguationData":[OSD([sQuery(id+"F0.wireOp",EDGE,"E1.left")])],"isStart":true})}),-1.0]])]});
            var Q1;
            Q1=makeQuery(id+"F16.imprint","IMPRINT",FACE,{"disambiguationData":[TD([[makeQuery(id+"F16.imprint","IMPRINT",EDGE,{"derivedFrom":sQuery(id+"F16.wireOp",EDGE,"E80")}),-1.0]])]});
            var Q2;
            {var subQ0=sQuery(id+"F16.wireOp",EDGE,"E87.MirrorCS");Q2=makeQuery(id+"F16.imprint","IMPRINT",FACE,{"disambiguationData":[TD([[makeQuery(id+"F16.imprint","IMPRINT",EDGE,{"derivedFrom":subQ0}),1.0]])]});}
            var Q3;
            Q3=makeQuery(id+"F2.opExtrude","CAP_FACE",FACE,{"disambiguationData":[OSD([sQuery(id+"F0.wireOp",EDGE,"E12"),sQuery(id+"F0.wireOp",EDGE,"E13"),sQuery(id+"F0.wireOp",EDGE,"E14"),sQuery(id+"F0.wireOp",EDGE,"E15"),sQuery(id+"F0.wireOp",EDGE,"E17.filletArc"),sQuery(id+"F0.wireOp",EDGE,"E18.filletArc"),sQuery(id+"F0.wireOp",EDGE,"E19.filletArc"),sQuery(id+"F0.wireOp",EDGE,"E20.filletArc"),sQuery(id+"F0.wireOp",EDGE,"E25.0"),sQuery(id+"F0.wireOp",EDGE,"E25.1"),sQuery(id+"F0.wireOp",EDGE,"E25.2"),sQuery(id+"F0.wireOp",EDGE,"E25.3"),sQuery(id+"F0.wireOp",EDGE,"E25.4"),sQuery(id+"F0.wireOp",EDGE,"E25.5"),sQuery(id+"F0.wireOp",EDGE,"E25.6"),sQuery(id+"F0.wireOp",EDGE,"E25.7")])],"isStart":false});
            extrude(context, id + "F17", {"entities" : qUnion([Q0, Q1, Q2]), "endBound" : BoundingType.UP_TO_SURFACE, "endBoundEntityFace" : qUnion([Q3]), "depth" : 25 * mm});
        }
    });
